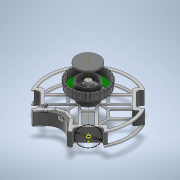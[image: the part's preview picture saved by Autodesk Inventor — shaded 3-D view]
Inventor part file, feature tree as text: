
AUTODESK INVENTOR PART (.ipt)
format: ipt  version: 2020 (Build 240168000, 168)  size: 2,160,128 bytes
history: native  units: mm
features: sketch x21, extrude x19, other x13, projected_geometry x4, pattern_circular x2, revolve x1
ambient origin geometry x8: Origin, YZ Plane, XZ Plane, XY Plane, X Axis, Y Axis, Z Axis, Center Point
bodies: Body1 (feature_tree)
feature tree (60):
  other  "Твердое тело1"
  other  "bottom_frame"
  other  "motowheels"
  extrude  "catcher"  Depth=88.0mm
  sketch  "Эскиз4"
  extrude  "Выдавливание2"  Depth=7.0mm
  extrude  "Выдавливание3"  Depth=5.0mm
  extrude  "Выдавливание21"  Depth=7.0mm
  other  "РабПлоскость1"
  extrude  "Выдавливание6"  Depth=5.0mm
  sketch  "Эскиз8"
  other  "РабПлоскость2"
  sketch  "Эскиз11"
  sketch  "Эскиз12"
  other  "РабПлоскость3"
  sketch  "Эскиз18"
  sketch  "Эскиз19"
  extrude  "Выдавливание15"  Depth=7.0mm
  extrude  "Выдавливание16"  Depth=5.0mm
  other  "РабПлоскость7"
  sketch  "Эскиз22"
  other  "РабПлоскость9"
  sketch  "Эскиз25"
  other  "РабПлоскость10"
  revolve  "Вращение2"
  sketch  "Эскиз29"
  extrude  "Выдавливание20"  Depth=5.1mm
  pattern_circular  "Круговой массив3"  Count=3  [1 undecoded]
  other  "РабПлоскость11"
  extrude  "Выдавливание22"  Depth=7.5mm
  other  "upper_frame"
  sketch  "Эскиз33"
  extrude  "Выдавливание23"  Depth=11.2mm
  sketch  "Эскиз34"
  other  "РабПлоскость12"
  extrude  "Выдавливание24"  Depth=20.5mm
  sketch  "Эскиз36"
  extrude  "Выдавливание25"  Depth=7.0mm TaperAngle=0.0deg
  extrude  "Выдавливание26"  Depth=4.0mm TaperAngle=0.0deg
  extrude  "Выдавливание27"  Depth=7.6mm
  pattern_circular  "Круговой массив4"  [2 undecoded]
  sketch  "Эскиз38"
  extrude  "Выдавливание28"  Depth=10.0mm
  extrude  "Выдавливание29"  Depth=15.0mm
  extrude  "Выдавливание30"  Depth=20.0mm TaperAngle=0.0deg
  sketch  "Эскиз40"
  other  "РабПлоскость13"
  extrude  "Выдавливание32"  Depth=3.0mm
  extrude  "Выдавливание33"  Depth=6.0mm
  sketch  "Эскиз7"
  projected_geometry  "Спроецированная петля1"
  sketch  "Эскиз26"
  projected_geometry  "Спроецированная петля2"
  sketch  "Эскиз30"
  projected_geometry  "Спроецированная петля3"
  projected_geometry  "Спроецированная петля4"
  sketch  "Эскиз35"
  sketch  "Эскиз37"
  sketch  "Эскиз39"
  sketch  "Эскиз41"
note: 3 required parameter values undecoded (feature->parameter linkage not recoverable at this tier; creation-order binding heuristic only, values carry confidence <= 0.55)
